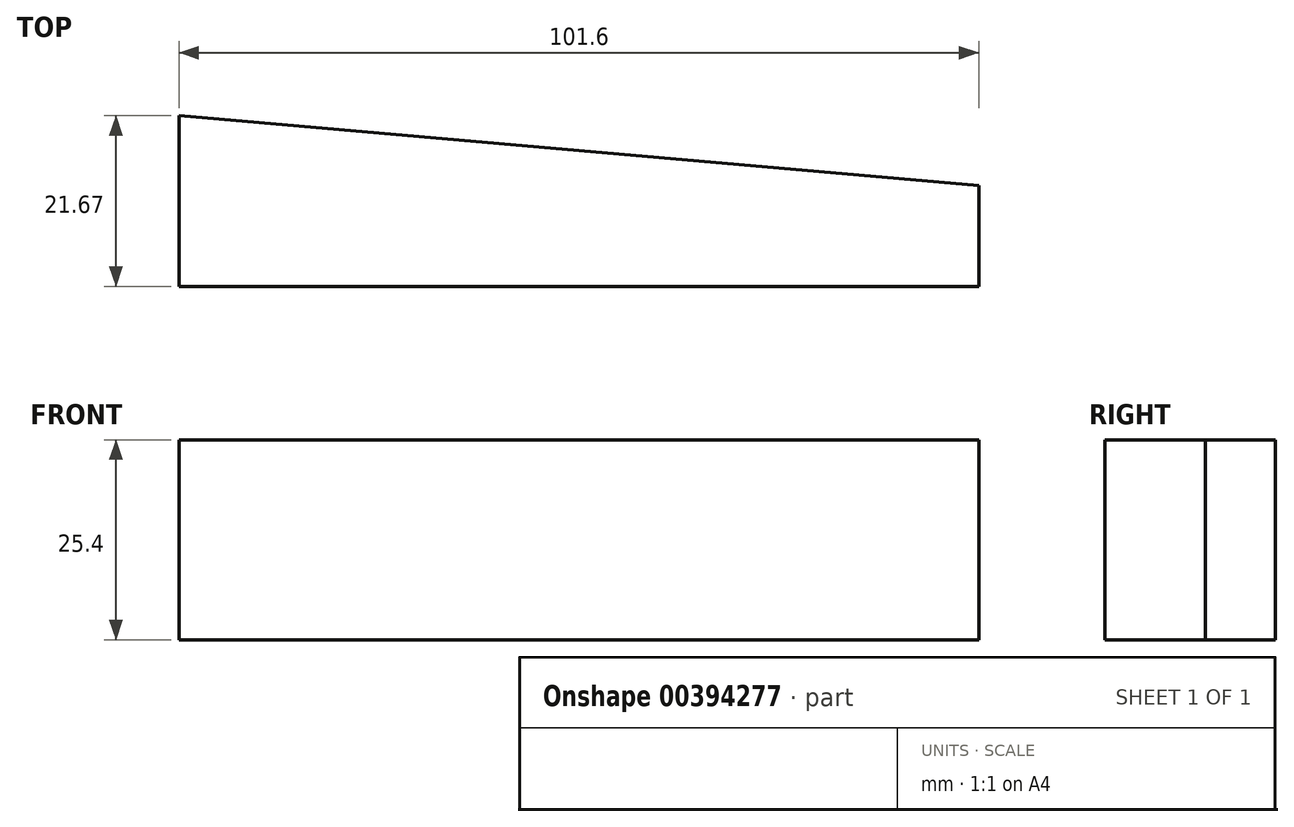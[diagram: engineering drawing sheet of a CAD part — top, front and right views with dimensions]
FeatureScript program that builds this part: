
annotation { "Feature Type Name" : "Feature", "Feature Type Description" : "" }
export const myFeature = defineFeature(function(context is Context, id is Id, definition is map)
    precondition{}
    {
        {
            var Q0;
            Q0=qCreatedBy(makeId("Top.planeOp"),FACE);
            var sketch = newSketch(context, id + "F0", { "sketchPlane" : qUnion([Q0])});
            skLineSegment(sketch, "E0", {"start": v(196.85, 0) * mm, "end": v(-50.8, 0) * mm});
            skLineSegment(sketch, "E1", {"start": v(-50.8, 0) * mm, "end": v(-50.8, 21.67) * mm});
            skLineSegment(sketch, "E2", {"start": v(-50.8, 21.67) * mm, "end": v(196.85, 0) * mm});
            skLineSegment(sketch, "E3", {"start": v(50.8, 12.78) * mm, "end": v(50.8, 0) * mm});
            skSolve(sketch);
        }
        {
            var Q0;
            {var subQ0=sQuery(id+"F0.wireOp",EDGE,"E1");Q0=makeQuery(id+"F0.imprint","IMPRINT",FACE,{"disambiguationData":[TD([[makeQuery(id+"F0.imprint","IMPRINT",EDGE,{"derivedFrom":subQ0}),-1.0]])]});}
            extrude(context, id + "F1", {"entities" : qUnion([Q0]), "depth" : 25.4 * mm});
        }
    });
